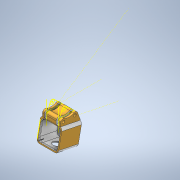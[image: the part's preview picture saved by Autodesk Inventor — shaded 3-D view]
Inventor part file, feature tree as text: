
AUTODESK INVENTOR PART (.ipt)
format: ipt  version: 2020 (Build 240168000, 168)  size: 361,472 bytes
history: native  units: mm
features: projected_geometry x6, sketch x5, other x4, extrude x1
ambient origin geometry x8: Origin, YZ Plane, XZ Plane, XY Plane, X Axis, Y Axis, Z Axis, Center Point
bodies: Solid1 (feature_tree)
feature tree (16):
  other  "V2 modular session micro cam adj mount 45 deg.iam"
  other  "V2 session mount 45deg block.ipt:1"
  other  "Kauri modular camera mount HDzero micro v1.ipt:1"
  other  "Kauri modular camera mount HDzero micro v1.ipt:2"
  extrude  "Extrusion1"  TaperAngle=0.0deg  [1 undecoded]
  sketch  "Sketch6"
  sketch  "Sketch7"
  sketch  "Sketch2"  dims[d3=0.2mm]
  sketch  "Sketch2_1"  dims[d0=10.0mm d1=0.0mm d2=0.0mm]
  sketch  "Sketch5"
  projected_geometry  "Projected Loop1"
  projected_geometry  "Projected Loop2"
  projected_geometry  "Projected Loop3"
  projected_geometry  "Projected Loop4"
  projected_geometry  "Projected Loop5"
  projected_geometry  "Projected Loop6"
note: 1 required parameter value undecoded (feature->parameter linkage not recoverable at this tier; creation-order binding heuristic only, values carry confidence <= 0.55)
